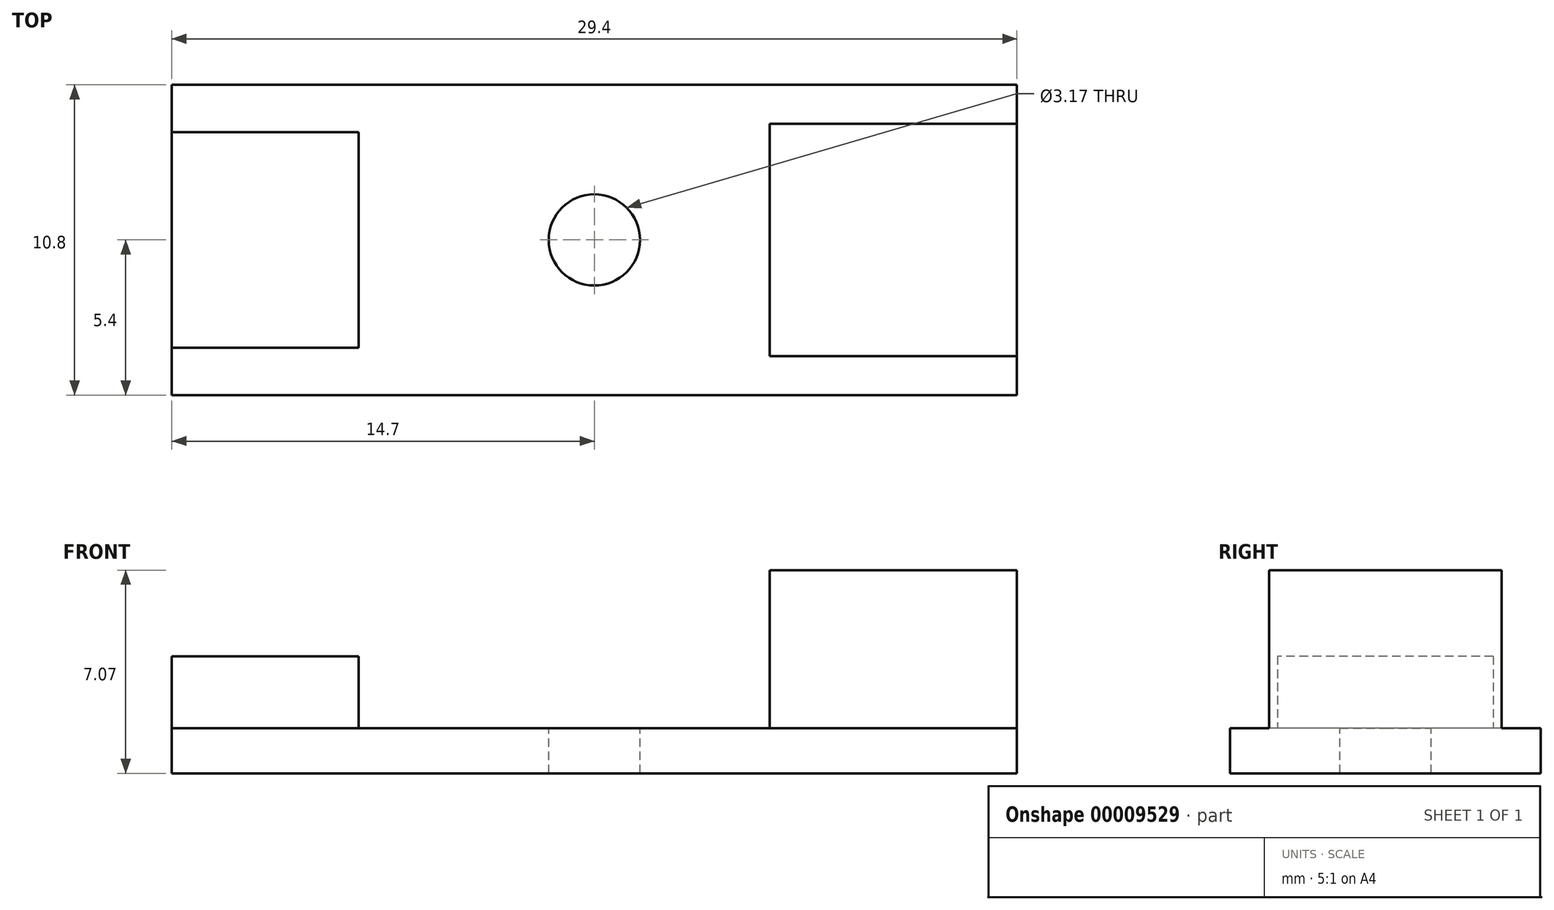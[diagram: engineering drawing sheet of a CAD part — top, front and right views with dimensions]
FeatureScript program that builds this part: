
annotation { "Feature Type Name" : "Feature", "Feature Type Description" : "" }
export const myFeature = defineFeature(function(context is Context, id is Id, definition is map)
    precondition{}
    {
        {
            var Q0;
            Q0=qCreatedBy(makeId("Top.planeOp"),FACE);
            var sketch = newSketch(context, id + "F0", { "sketchPlane" : qUnion([Q0])});
            skLineSegment(sketch, "E0.rect.bottom", {"start": v(14.7, 5.4) * mm, "end": v(-14.7, 5.4) * mm});
            skLineSegment(sketch, "E0.rect.top", {"start": v(14.7, -5.4) * mm, "end": v(-14.7, -5.4) * mm});
            skLineSegment(sketch, "E0.rect.left", {"start": v(14.7, 5.4) * mm, "end": v(14.7, -5.4) * mm});
            skLineSegment(sketch, "E0.rect.right", {"start": v(-14.7, 5.4) * mm, "end": v(-14.7, -5.4) * mm});
            skPoint(sketch, "E0.rect.middle", {"position": v(0, 0) * mm});
            skSolve(sketch);
        }
        {
            var Q0;
            Q0=makeQuery(id+"F0.imprint","IMPRINT",FACE,{"disambiguationData":[TD([[makeQuery(id+"F0.imprint","IMPRINT",EDGE,{"derivedFrom":sQuery(id+"F0.wireOp",EDGE,"E0.rect.bottom")}),1.0]])]});
            extrude(context, id + "F1", {"entities" : qUnion([Q0]), "depth" : 1.57 * mm});
        }
        {
            var Q0;
            Q0=makeQuery(id+"F1.opExtrude","CAP_FACE",FACE,{"disambiguationData":[OSD([sQuery(id+"F0.wireOp",EDGE,"E0.rect.bottom"),sQuery(id+"F0.wireOp",EDGE,"E0.rect.top"),sQuery(id+"F0.wireOp",EDGE,"E0.rect.left"),sQuery(id+"F0.wireOp",EDGE,"E0.rect.right")])],"isStart":false});
            var sketch = newSketch(context, id + "F2", { "sketchPlane" : qUnion([Q0])});
            skLineSegment(sketch, "E1.rect.bottom", {"start": v(14.7, 4.05) * mm, "end": v(6.1, 4.05) * mm});
            skLineSegment(sketch, "E1.rect.top", {"start": v(14.7, -4.05) * mm, "end": v(6.1, -4.05) * mm});
            skLineSegment(sketch, "E1.rect.left", {"start": v(14.7, 4.05) * mm, "end": v(14.7, -4.05) * mm});
            skLineSegment(sketch, "E1.rect.right", {"start": v(6.1, 4.05) * mm, "end": v(6.1, -4.05) * mm});
            skPoint(sketch, "E1.rect.middle", {"position": v(10.4, 0) * mm});
            skSolve(sketch);
        }
        {
            var Q0;
            Q0=makeQuery(id+"F2.imprint","IMPRINT",FACE,{"disambiguationData":[TD([[makeQuery(id+"F2.imprint","IMPRINT",EDGE,{"derivedFrom":sQuery(id+"F2.wireOp",EDGE,"E1.rect.bottom")}),1.0]])]});
            extrude(context, id + "F3", {"entities" : qUnion([Q0]), "operationType" : NewBodyOperationType.ADD, "depth" : 5.5 * mm});
        }
        {
            var Q0;
            Q0=makeQuery(id+"F1.opExtrude","CAP_FACE",FACE,{"disambiguationData":[OSD([sQuery(id+"F0.wireOp",EDGE,"E0.rect.bottom"),sQuery(id+"F0.wireOp",EDGE,"E0.rect.top"),sQuery(id+"F0.wireOp",EDGE,"E0.rect.left"),sQuery(id+"F0.wireOp",EDGE,"E0.rect.right")])],"isStart":false});
            var sketch = newSketch(context, id + "F4", { "sketchPlane" : qUnion([Q0])});
            skLineSegment(sketch, "E2.rect.bottom", {"start": v(-14.7, 3.75) * mm, "end": v(-8.2, 3.75) * mm});
            skLineSegment(sketch, "E2.rect.top", {"start": v(-14.7, -3.75) * mm, "end": v(-8.2, -3.75) * mm});
            skLineSegment(sketch, "E2.rect.left", {"start": v(-14.7, 3.75) * mm, "end": v(-14.7, -3.75) * mm});
            skLineSegment(sketch, "E2.rect.right", {"start": v(-8.2, 3.75) * mm, "end": v(-8.2, -3.75) * mm});
            skPoint(sketch, "E2.rect.middle", {"position": v(-11.45, 0) * mm});
            skSolve(sketch);
        }
        {
            var Q0;
            Q0 = qSketchRegion(id + "F4", true);
            extrude(context, id + "F5", {"entities" : qUnion([Q0]), "operationType" : NewBodyOperationType.ADD, "depth" : 2.5 * mm});
        }
        {
            var Q0;
            Q0=makeQuery(id+"F1.opExtrude","CAP_FACE",FACE,{"disambiguationData":[OSD([sQuery(id+"F0.wireOp",EDGE,"E0.rect.bottom"),sQuery(id+"F0.wireOp",EDGE,"E0.rect.top"),sQuery(id+"F0.wireOp",EDGE,"E0.rect.left"),sQuery(id+"F0.wireOp",EDGE,"E0.rect.right")])],"isStart":false});
            var sketch = newSketch(context, id + "F6", { "sketchPlane" : qUnion([Q0])});
            skCircle(sketch, "E3", {"center": v(0, 0) * mm, "radius": 1.59 * mm});
            skSolve(sketch);
        }
        {
            var Q0;
            Q0=makeQuery(id+"F6.imprint","IMPRINT",FACE,{"disambiguationData":[TD([[makeQuery(id+"F6.imprint","IMPRINT",EDGE,{"derivedFrom":sQuery(id+"F6.wireOp",EDGE,"E3")}),1.0]])]});
            extrude(context, id + "F7", {"entities" : qUnion([Q0]), "operationType" : NewBodyOperationType.REMOVE, "endBound" : BoundingType.THROUGH_ALL, "oppositeDirection" : true, "depth" : 25.4 * mm});
        }
    });
